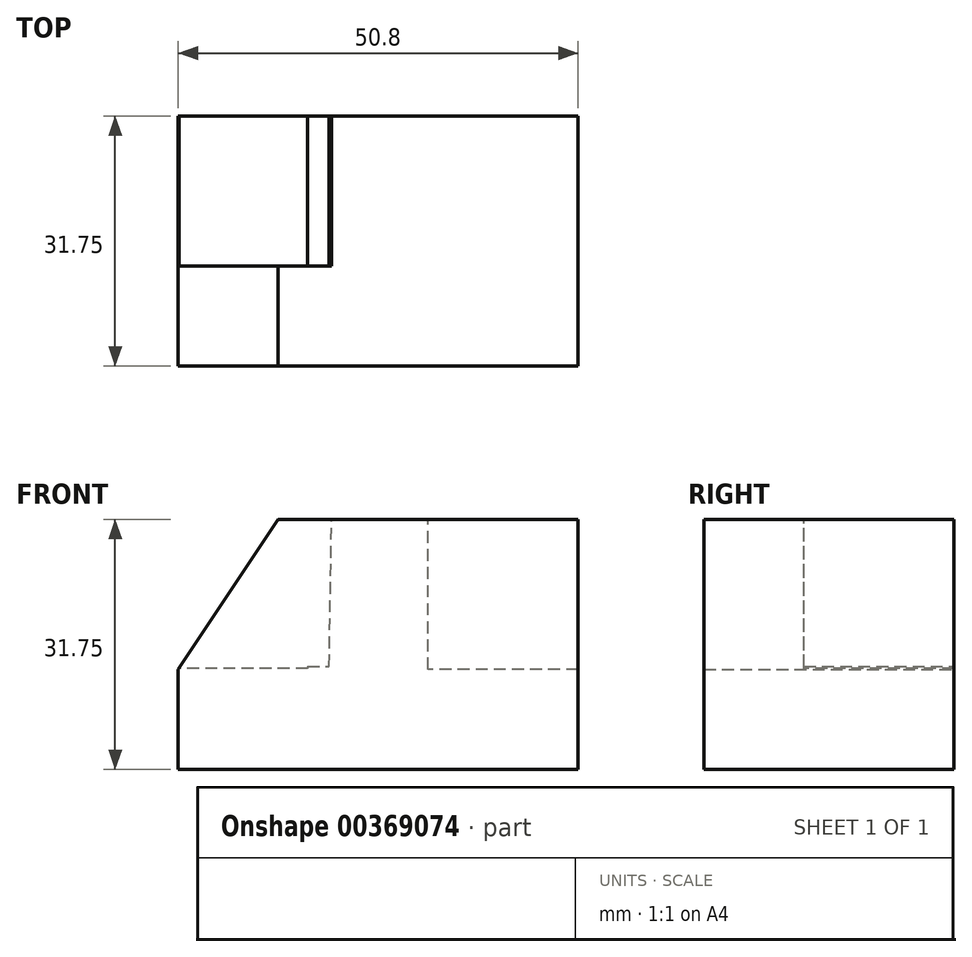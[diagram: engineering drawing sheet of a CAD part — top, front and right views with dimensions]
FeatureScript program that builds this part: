
annotation { "Feature Type Name" : "Feature", "Feature Type Description" : "" }
export const myFeature = defineFeature(function(context is Context, id is Id, definition is map)
    precondition{}
    {
        {
            var Q0;
            Q0=qCreatedBy(makeId("Front.planeOp"),FACE);
            var sketch = newSketch(context, id + "F0", { "sketchPlane" : qUnion([Q0])});
            skLineSegment(sketch, "E0", {"start": v(0, 0) * mm, "end": v(-50.8, 0) * mm});
            skLineSegment(sketch, "E1", {"start": v(-50.8, 0) * mm, "end": v(-50.8, 12.7) * mm});
            skLineSegment(sketch, "E2", {"start": v(-50.8, 12.7) * mm, "end": v(-38.1, 31.75) * mm});
            skLineSegment(sketch, "E3", {"start": v(-38.1, 31.75) * mm, "end": v(0, 31.75) * mm});
            skLineSegment(sketch, "E4", {"start": v(0, 31.75) * mm, "end": v(0, 0) * mm});
            skSolve(sketch);
        }
        {
            var Q0;
            Q0=makeQuery(id+"F0.imprint","IMPRINT",FACE,{"disambiguationData":[TD([[makeQuery(id+"F0.imprint","IMPRINT",EDGE,{"derivedFrom":sQuery(id+"F0.wireOp",EDGE,"E0")}),-1.0]])]});
            extrude(context, id + "F1", {"entities" : qUnion([Q0]), "depth" : 31.75 * mm});
        }
        {
            var Q0;
            Q0=qCreatedBy(makeId("Front.planeOp"),FACE);
            var sketch = newSketch(context, id + "F2", { "sketchPlane" : qUnion([Q0])});
            skLineSegment(sketch, "E5", {"start": v(0, 12.7) * mm, "end": v(-19.05, 12.7) * mm});
            skLineSegment(sketch, "E6", {"start": v(-19.05, 12.7) * mm, "end": v(-19.05, 31.75) * mm});
            skLineSegment(sketch, "E7", {"start": v(-19.05, 31.75) * mm, "end": v(0, 31.75) * mm});
            skLineSegment(sketch, "E8", {"start": v(0, 31.75) * mm, "end": v(0, 12.7) * mm});
            skSolve(sketch);
        }
        {
            var Q0;
            Q0=makeQuery(id+"F2.imprint","IMPRINT",FACE,{"disambiguationData":[TD([[makeQuery(id+"F2.imprint","IMPRINT",EDGE,{"derivedFrom":sQuery(id+"F2.wireOp",EDGE,"E5")}),-1.0]])]});
            extrude(context, id + "F3", {"entities" : qUnion([Q0]), "operationType" : NewBodyOperationType.REMOVE, "depth" : 3 / 101.6 * mm});
        }
        {
            var Q0;
            Q0=qCreatedBy(makeId("Front.planeOp"),FACE);
            var sketch = newSketch(context, id + "F4", { "sketchPlane" : qUnion([Q0])});
            skLineSegment(sketch, "E9", {"start": v(-31.3, 32.14) * mm, "end": v(-37.65, 32.14) * mm});
            skLineSegment(sketch, "E10", {"start": v(-37.65, 32.14) * mm, "end": v(-50.67, 13.1) * mm});
            skLineSegment(sketch, "E11", {"start": v(-50.67, 13.1) * mm, "end": v(-31.62, 13.1) * mm});
            skLineSegment(sketch, "E12", {"start": v(-31.62, 13.1) * mm, "end": v(-31.3, 32.14) * mm});
            skSolve(sketch);
        }
        {
            var Q0;
            Q0=makeQuery(id+"F4.imprint","IMPRINT",FACE,{"disambiguationData":[TD([[makeQuery(id+"F4.imprint","IMPRINT",EDGE,{"derivedFrom":sQuery(id+"F4.wireOp",EDGE,"E9")}),1.0]])]});
            extrude(context, id + "F5", {"entities" : qUnion([Q0]), "operationType" : NewBodyOperationType.REMOVE, "depth" : 19.05 * mm});
        }
        {
            var Q0;
            Q0=qCreatedBy(makeId("Front.planeOp"),FACE);
            var sketch = newSketch(context, id + "F6", { "sketchPlane" : qUnion([Q0])});
            skLineSegment(sketch, "E13", {"start": v(-34.36, 37.6) * mm, "end": v(-34.36, 12.84) * mm});
            skLineSegment(sketch, "E14", {"start": v(-34.36, 12.84) * mm, "end": v(-68.1, 12.84) * mm});
            skLineSegment(sketch, "E15", {"start": v(-68.1, 12.84) * mm, "end": v(-31.57, 37.6) * mm});
            skSolve(sketch);
        }
        {
            var Q0;
            Q0 = qSketchRegion(id + "F6", true);
            extrude(context, id + "F7", {"entities" : qUnion([Q0]), "operationType" : NewBodyOperationType.REMOVE, "depth" : 19.05 * mm});
        }
    });
